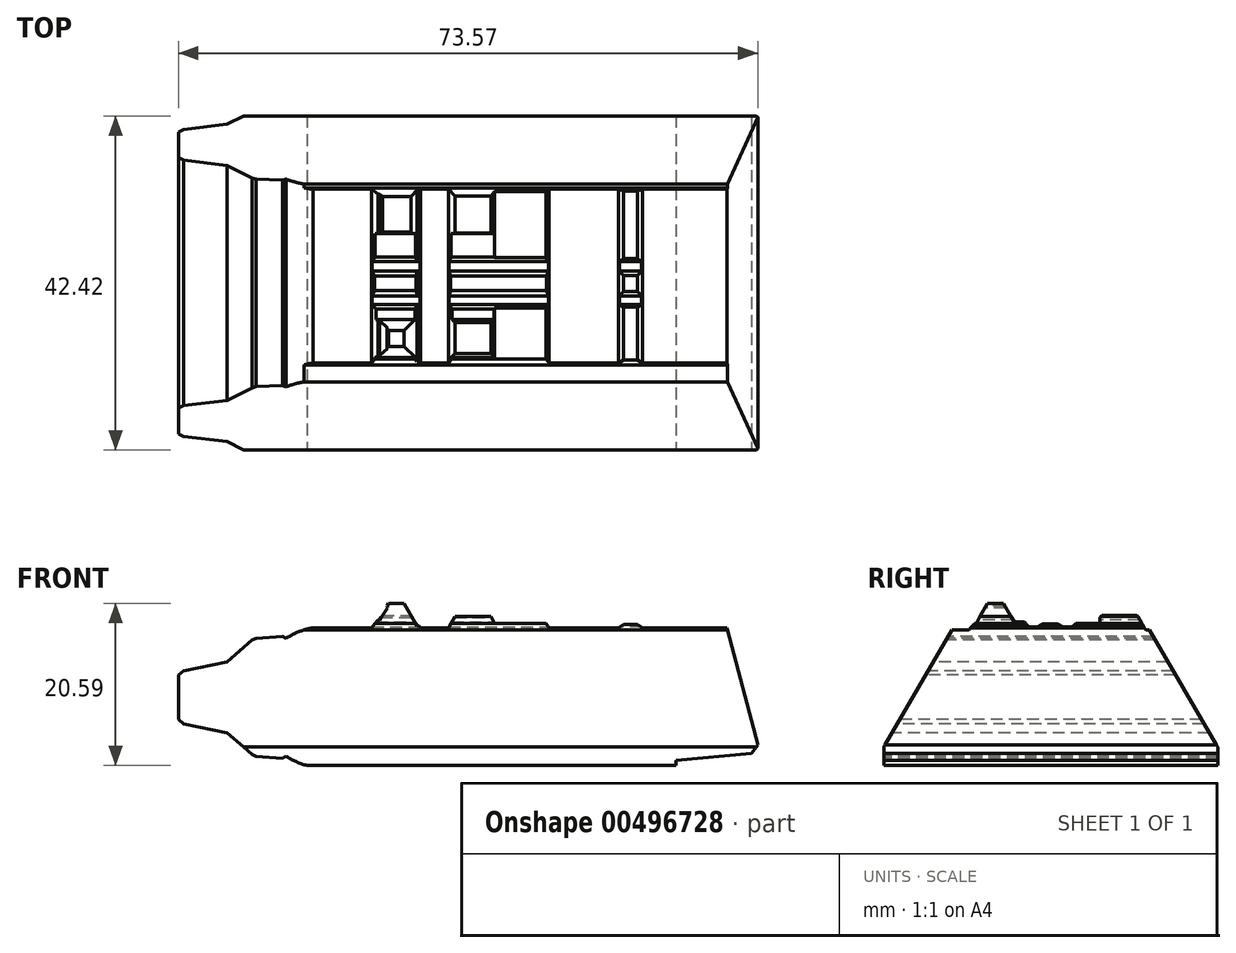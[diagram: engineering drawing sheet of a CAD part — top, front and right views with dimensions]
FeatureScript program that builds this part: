
annotation { "Feature Type Name" : "Feature", "Feature Type Description" : "" }
export const myFeature = defineFeature(function(context is Context, id is Id, definition is map)
    precondition{}
    {
        {
            var Q0;
            Q0=qCreatedBy(makeId("Top.planeOp"),FACE);
            var sketch = newSketch(context, id + "F0", { "sketchPlane" : qUnion([Q0])});
            skLineSegment(sketch, "E0", {"start": v(30.01, -20.73) * mm, "end": v(-121.62, -20.73) * mm, "construction": true});
            skLineSegment(sketch, "E1", {"start": v(-11.64, 108.22) * mm, "end": v(32.5, 108.22) * mm, "construction": true});
            skLineSegment(sketch, "E2", {"start": v(19.72, 67.84) * mm, "end": v(19.72, 108.22) * mm, "construction": true});
            skLineSegment(sketch, "E3", {"start": v(3.91, 88.98) * mm, "end": v(38.78, 88.98) * mm, "construction": true});
            skLineSegment(sketch, "E4", {"start": v(19.72, 67.84) * mm, "end": v(19.72, 88.98) * mm, "construction": true});
            skLineSegment(sketch, "E5", {"start": v(10.58, 90.44) * mm, "end": v(38.78, 90.44) * mm, "construction": true});
            skLineSegment(sketch, "E6", {"start": v(19.72, 90.44) * mm, "end": v(19.72, 67.84) * mm});
            skPoint(sketch, "E7", {"position": v(18.71, -41.94) * mm});
            skLineSegment(sketch, "E8", {"start": v(18.71, -41.94) * mm, "end": v(-45.8, -41.94) * mm});
            skLineSegment(sketch, "E9", {"start": v(-45.8, -41.94) * mm, "end": v(-45.8, -20.73) * mm});
            skLineSegment(sketch, "E10", {"start": v(18.71, -41.94) * mm, "end": v(18.71, -20.73) * mm});
            skLineSegment(sketch, "E11", {"start": v(18.71, -20.73) * mm, "end": v(-45.8, -20.73) * mm});
            skLineSegment(sketch, "E12.MirrorCS", {"start": v(-45.8, 0.48) * mm, "end": v(-45.8, -20.73) * mm});
            skLineSegment(sketch, "E13.MirrorCS", {"start": v(18.71, 0.48) * mm, "end": v(-45.8, 0.48) * mm});
            skLineSegment(sketch, "E14.MirrorCS", {"start": v(18.71, 0.48) * mm, "end": v(18.71, -20.73) * mm});
            skLineSegment(sketch, "E15", {"start": v(-56.07, -20.73) * mm, "end": v(-56.07, -41.94) * mm});
            skLineSegment(sketch, "E16", {"start": v(-56.07, -41.94) * mm, "end": v(-45.8, -41.94) * mm});
            skLineSegment(sketch, "E17.MirrorCS", {"start": v(-56.07, -20.73) * mm, "end": v(-56.07, 0.48) * mm});
            skLineSegment(sketch, "E18.MirrorCS", {"start": v(-56.07, 0.48) * mm, "end": v(-45.8, 0.48) * mm});
            skSolve(sketch);
        }
        {
            var Q0;
            Q0=makeQuery(id+"F0.imprint","IMPRINT",FACE,{"disambiguationData":[TD([[makeQuery(id+"F0.imprint","IMPRINT",EDGE,{"derivedFrom":sQuery(id+"F0.wireOp",EDGE,"E11")}),-1.0]])]});
            var Q1;
            Q1=makeQuery(id+"F0.imprint","IMPRINT",FACE,{"disambiguationData":[TD([[makeQuery(id+"F0.imprint","IMPRINT",EDGE,{"derivedFrom":sQuery(id+"F0.wireOp",EDGE,"E8")}),-1.0]])]});
            var Q2;
            Q2=makeQuery(id+"F0.imprint","IMPRINT",FACE,{"disambiguationData":[TD([[makeQuery(id+"F0.imprint","IMPRINT",EDGE,{"derivedFrom":sQuery(id+"F0.wireOp",EDGE,"E9")}),1.0]])]});
            extrude(context, id + "F1", {"entities" : qUnion([Q0, Q1, Q2]), "depth" : 25.4 * mm});
        }
        {
            var Q0;
            Q0=makeQuery(id+"F1.opExtrude","SWEPT_FACE",FACE,{"disambiguationData":[OSD([sQuery(id+"F0.wireOp",EDGE,"E8")])]});
            var sketch = newSketch(context, id + "F2", { "sketchPlane" : qUnion([Q0])});
            skLineSegment(sketch, "E19", {"start": v(-38.72, 17.5) * mm, "end": v(13.85, 17.5) * mm});
            skLineSegment(sketch, "E20", {"start": v(13.85, 17.5) * mm, "end": v(17.78, 2.64) * mm});
            skLineSegment(sketch, "E21", {"start": v(17.78, 2.64) * mm, "end": v(17.01, 1.56) * mm});
            skLineSegment(sketch, "E22", {"start": v(17.01, 1.56) * mm, "end": v(7.37, 0.66) * mm});
            skLineSegment(sketch, "E23", {"start": v(7.37, 0.66) * mm, "end": v(7.37, -0.21) * mm});
            skLineSegment(sketch, "E24", {"start": v(7.37, -0.21) * mm, "end": v(-38.4, -0.21) * mm});
            skArc(sketch, "E25", {"start": v(-38.72, 17.5) * mm, "mid": v(-46.17, 8.5) * mm, "end": v(-38.4, -0.21) * mm});
            skLineSegment(sketch, "E26", {"start": v(-37.2, 8.67) * mm, "end": v(-57.94, 8.67) * mm, "construction": true});
            skLineSegment(sketch, "E27", {"start": v(-42.17, 16.13) * mm, "end": v(-42.58, 16.41) * mm});
            skLineSegment(sketch, "E28", {"start": v(-42.61, 16.42) * mm, "end": v(-45.95, 16.16) * mm});
            skPoint(sketch, "E29.visualSharp", {"position": v(-42.6, 16.42) * mm});
            skArc(sketch, "E29.filletArc", {"start": v(-42.58, 16.41) * mm, "mid": v(-42.6, 16.42) * mm, "end": v(-42.61, 16.42) * mm});
            skLineSegment(sketch, "E30.MirrorCS", {"start": v(-42.61, 0.91) * mm, "end": v(-45.95, 1.17) * mm});
            skLineSegment(sketch, "E31.MirrorCS", {"start": v(-42.17, 1.2) * mm, "end": v(-42.58, 0.92) * mm});
            skArc(sketch, "E32", {"start": v(-44.02, 16.31) * mm, "mid": v(-47.2, 8.7) * mm, "end": v(-44.15, 1.03) * mm});
            skArc(sketch, "E33", {"start": v(-45.95, 16.16) * mm, "mid": v(-48.83, 8.67) * mm, "end": v(-45.95, 1.17) * mm});
            skLineSegment(sketch, "E34", {"start": v(-45.95, 16.16) * mm, "end": v(-46.43, 15.92) * mm});
            skLineSegment(sketch, "E35", {"start": v(-46.43, 15.92) * mm, "end": v(-49.61, 13.17) * mm});
            skLineSegment(sketch, "E36", {"start": v(-49.61, 13.17) * mm, "end": v(-55.16, 12.03) * mm});
            skLineSegment(sketch, "E37", {"start": v(-55.16, 12.03) * mm, "end": v(-55.79, 11.48) * mm});
            skLineSegment(sketch, "E38", {"start": v(-55.79, 11.48) * mm, "end": v(-55.79, 8.67) * mm});
            skLineSegment(sketch, "E39.MirrorCS", {"start": v(-49.61, 4.17) * mm, "end": v(-55.16, 5.3) * mm});
            skLineSegment(sketch, "E40.MirrorCS", {"start": v(-55.16, 5.3) * mm, "end": v(-55.79, 5.85) * mm});
            skLineSegment(sketch, "E41.MirrorCS", {"start": v(-55.79, 5.85) * mm, "end": v(-55.79, 8.67) * mm});
            skLineSegment(sketch, "E42.MirrorCS", {"start": v(-46.43, 1.41) * mm, "end": v(-49.61, 4.17) * mm});
            skLineSegment(sketch, "E43.MirrorCS", {"start": v(-45.95, 1.17) * mm, "end": v(-46.43, 1.41) * mm});
            skLineSegment(sketch, "E44", {"start": v(-31.25, 17.5) * mm, "end": v(-30.46, 18.52) * mm});
            skLineSegment(sketch, "E45", {"start": v(-30.46, 18.52) * mm, "end": v(-30.28, 18.52) * mm});
            skLineSegment(sketch, "E46", {"start": v(-30.28, 18.52) * mm, "end": v(-29.25, 20.03) * mm});
            skLineSegment(sketch, "E47", {"start": v(-29.25, 20.03) * mm, "end": v(-29.34, 20.3) * mm});
            skLineSegment(sketch, "E48", {"start": v(-29.34, 20.3) * mm, "end": v(-29.12, 20.59) * mm});
            skLineSegment(sketch, "E49", {"start": v(-29.12, 20.59) * mm, "end": v(-27.14, 20.59) * mm});
            skLineSegment(sketch, "E50", {"start": v(-27.14, 20.59) * mm, "end": v(-25.47, 17.7) * mm});
            skLineSegment(sketch, "E51", {"start": v(-25.47, 17.7) * mm, "end": v(-25.23, 17.7) * mm});
            skLineSegment(sketch, "E52", {"start": v(-25.23, 17.7) * mm, "end": v(-25.05, 17.5) * mm});
            skLineSegment(sketch, "E53", {"start": v(-21.5, 17.5) * mm, "end": v(-20.66, 18.93) * mm});
            skLineSegment(sketch, "E54", {"start": v(-20.66, 18.93) * mm, "end": v(-16.12, 18.93) * mm});
            skLineSegment(sketch, "E55", {"start": v(-16.12, 18.93) * mm, "end": v(-15.63, 18.04) * mm});
            skLineSegment(sketch, "E56", {"start": v(-15.63, 18.04) * mm, "end": v(-9.11, 18.04) * mm});
            skLineSegment(sketch, "E57", {"start": v(-9.11, 18.04) * mm, "end": v(-8.75, 17.5) * mm});
            skLineSegment(sketch, "E58", {"start": v(0.11, 17.5) * mm, "end": v(0.72, 17.92) * mm});
            skLineSegment(sketch, "E59", {"start": v(0.72, 17.92) * mm, "end": v(2.53, 17.92) * mm});
            skLineSegment(sketch, "E60", {"start": v(2.53, 17.92) * mm, "end": v(3.15, 17.5) * mm});
            skLineSegment(sketch, "E61", {"start": v(-45.95, 16.16) * mm, "end": v(-42.58, 16.41) * mm});
            skLineSegment(sketch, "E62", {"start": v(-45.95, 1.17) * mm, "end": v(-42.58, 0.92) * mm});
            skLineSegment(sketch, "E63", {"start": v(-55.16, 12.03) * mm, "end": v(-49.61, 13.17) * mm});
            skLineSegment(sketch, "E64", {"start": v(-45.95, 16.16) * mm, "end": v(-42.61, 16.42) * mm});
            skSolve(sketch);
        }
        {
            var Q0;
            {var subQ1=sQuery(id+"F2.wireOp",EDGE,"E30.MirrorCS");var subQ3=sQuery(id+"F2.wireOp",EDGE,"E32");var subQ4=makeQuery(id+"F2.imprint","INTERSECT",VERTEX,{"derivedFrom":[subQ1,subQ3]});Q0=makeQuery(id+"F2.imprint","IMPRINT",FACE,{"disambiguationData":[TD([[makeQuery(id+"F2.imprint","IMPRINT",EDGE,{"disambiguationData":[TD([[subQ4,1.0]])],"derivedFrom":subQ3}),-1.0]])]});}
            var Q1;
            {var subQ0=sQuery(id+"F2.wireOp",EDGE,"E29.filletArc");Q1=makeQuery(id+"F2.imprint","IMPRINT",FACE,{"disambiguationData":[TD([[makeQuery(id+"F2.imprint","IMPRINT",EDGE,{"derivedFrom":subQ0}),1.0]])]});}
            var Q2;
            {var subQ0=sQuery(id+"F2.wireOp",EDGE,"E64");var subQ1=sQuery(id+"F2.wireOp",EDGE,"E32");var subQ2=makeQuery(id+"F2.imprint","INTERSECT",VERTEX,{"derivedFrom":[subQ1,subQ0]});Q2=makeQuery(id+"F2.imprint","IMPRINT",FACE,{"disambiguationData":[TD([[makeQuery(id+"F2.imprint","IMPRINT",EDGE,{"disambiguationData":[TD([[subQ2,-1.0]])],"derivedFrom":subQ1}),-1.0]])]});}
            var Q3;
            {var subQ0=sQuery(id+"F2.wireOp",EDGE,"E24");Q3=makeQuery(id+"F2.imprint","IMPRINT",FACE,{"disambiguationData":[TD([[makeQuery(id+"F2.imprint","IMPRINT",EDGE,{"derivedFrom":subQ0}),-1.0]])]});}
            var Q4;
            {var subQ9=sQuery(id+"F2.wireOp",EDGE,"E20");Q4=makeQuery(id+"F2.imprint","IMPRINT",FACE,{"disambiguationData":[TD([[makeQuery(id+"F2.imprint","IMPRINT",EDGE,{"derivedFrom":subQ9}),1.0]])]});}
            extrude(context, id + "F3", {"entities" : qUnion([Q0, Q1, Q2, Q3, Q4]), "operationType" : NewBodyOperationType.REMOVE, "oppositeDirection" : true, "depth" : 51.82 * mm});
        }
        {
            var Q0;
            Q0=qCreatedBy(makeId("Right.planeOp"),FACE);
            var sketch = newSketch(context, id + "F4", { "sketchPlane" : qUnion([Q0])});
            skPoint(sketch, "E65.0", {"position": v(-20.73, 17.5) * mm});
            skLineSegment(sketch, "E66", {"start": v(-20.73, 17.5) * mm, "end": v(-20.73, -3.08) * mm, "construction": true});
            skLineSegment(sketch, "E67", {"start": v(-20.73, 17.23) * mm, "end": v(-33.29, 17.23) * mm});
            skLineSegment(sketch, "E68", {"start": v(-33.29, 17.23) * mm, "end": v(-42.28, 1.8) * mm});
            skLineSegment(sketch, "E69", {"start": v(-42.28, 1.8) * mm, "end": v(-42.28, -0.16) * mm});
            skLineSegment(sketch, "E70", {"start": v(-42.28, -0.16) * mm, "end": v(-42.08, -0.16) * mm});
            skLineSegment(sketch, "E71", {"start": v(-42.08, -0.16) * mm, "end": v(-42.08, -0.51) * mm});
            skLineSegment(sketch, "E72", {"start": v(-42.08, -0.51) * mm, "end": v(-20.73, -0.51) * mm});
            skLineSegment(sketch, "E73", {"start": v(-31.14, 17.23) * mm, "end": v(-30.37, 18.06) * mm});
            skLineSegment(sketch, "E74", {"start": v(-30.37, 18.06) * mm, "end": v(-30.19, 18.06) * mm});
            skLineSegment(sketch, "E75", {"start": v(-30.19, 18.06) * mm, "end": v(-28.74, 20.64) * mm});
            skLineSegment(sketch, "E76", {"start": v(-28.74, 20.64) * mm, "end": v(-26.79, 20.64) * mm});
            skLineSegment(sketch, "E77", {"start": v(-26.79, 20.64) * mm, "end": v(-25.34, 18.22) * mm});
            skLineSegment(sketch, "E78", {"start": v(-25.34, 18.22) * mm, "end": v(-24.06, 18.22) * mm});
            skLineSegment(sketch, "E79", {"start": v(-24.06, 18.22) * mm, "end": v(-23.46, 17.57) * mm});
            skLineSegment(sketch, "E80", {"start": v(-23.46, 17.57) * mm, "end": v(-23.46, 17.23) * mm});
            skLineSegment(sketch, "E81", {"start": v(-23.46, 17.57) * mm, "end": v(-22.4, 17.57) * mm});
            skLineSegment(sketch, "E82", {"start": v(-22.4, 17.57) * mm, "end": v(-21.72, 17.99) * mm});
            skLineSegment(sketch, "E83", {"start": v(-21.72, 17.99) * mm, "end": v(-19.87, 17.99) * mm});
            skLineSegment(sketch, "E84", {"start": v(-19.87, 17.99) * mm, "end": v(-19.2, 17.57) * mm});
            skLineSegment(sketch, "E85", {"start": v(-19.2, 17.57) * mm, "end": v(-18.01, 17.57) * mm});
            skLineSegment(sketch, "E86", {"start": v(-18.01, 17.57) * mm, "end": v(-17.46, 18.08) * mm});
            skLineSegment(sketch, "E87", {"start": v(-17.46, 18.08) * mm, "end": v(-14.46, 18.08) * mm});
            skLineSegment(sketch, "E88", {"start": v(-14.46, 18.08) * mm, "end": v(-14.46, 18.8) * mm});
            skLineSegment(sketch, "E89", {"start": v(-14.46, 18.8) * mm, "end": v(-14.25, 19.07) * mm});
            skLineSegment(sketch, "E90", {"start": v(-14.25, 19.07) * mm, "end": v(-9.75, 19.07) * mm});
            skLineSegment(sketch, "E91.MirrorCS", {"start": v(-20.73, 17.23) * mm, "end": v(-8.16, 17.23) * mm});
            skLineSegment(sketch, "E92.MirrorCS", {"start": v(-8.16, 17.23) * mm, "end": v(0.83, 1.8) * mm});
            skLineSegment(sketch, "E93.MirrorCS", {"start": v(0.83, 1.8) * mm, "end": v(0.83, -0.16) * mm});
            skLineSegment(sketch, "E94.MirrorCS", {"start": v(0.63, -0.16) * mm, "end": v(0.63, -0.51) * mm});
            skLineSegment(sketch, "E95.MirrorCS", {"start": v(0.63, -0.51) * mm, "end": v(-20.73, -0.51) * mm});
            skLineSegment(sketch, "E96", {"start": v(-9.75, 19.07) * mm, "end": v(-8.66, 17.23) * mm});
            skLineSegment(sketch, "E97", {"start": v(0.63, -0.16) * mm, "end": v(0.83, -0.16) * mm});
            skLineSegment(sketch, "E98", {"start": v(-42.28, 1.8) * mm, "end": v(-42.28, 21.25) * mm});
            skLineSegment(sketch, "E99", {"start": v(-42.28, 21.25) * mm, "end": v(1.26, 21.25) * mm});
            skLineSegment(sketch, "E100", {"start": v(1.26, 21.25) * mm, "end": v(0.83, 1.8) * mm});
            skLineSegment(sketch, "E101", {"start": v(0.83, -0.16) * mm, "end": v(0.83, -0.51) * mm});
            skLineSegment(sketch, "E102", {"start": v(0.83, -0.51) * mm, "end": v(0.63, -0.51) * mm});
            skLineSegment(sketch, "E103", {"start": v(-42.28, -0.16) * mm, "end": v(-42.28, -0.51) * mm});
            skLineSegment(sketch, "E104", {"start": v(-42.28, -0.51) * mm, "end": v(-42.08, -0.51) * mm});
            skSolve(sketch);
        }
        {
            var Q0;
            {var subQ4=sQuery(id+"F4.wireOp",EDGE,"E68");Q0=makeQuery(id+"F4.imprint","IMPRINT",FACE,{"disambiguationData":[TD([[makeQuery(id+"F4.imprint","IMPRINT",EDGE,{"derivedFrom":subQ4}),-1.0]])]});}
            extrude(context, id + "F5", {"entities" : qUnion([Q0]), "operationType" : NewBodyOperationType.REMOVE, "oppositeDirection" : true, "depth" : 78.49 * mm});
        }
        {
            var Q0;
            {var subQ4=sQuery(id+"F4.wireOp",EDGE,"E68");Q0=makeQuery(id+"F4.imprint","IMPRINT",FACE,{"disambiguationData":[TD([[makeQuery(id+"F4.imprint","IMPRINT",EDGE,{"derivedFrom":subQ4}),-1.0]])]});}
            extrude(context, id + "F6", {"entities" : qUnion([Q0]), "operationType" : NewBodyOperationType.REMOVE, "depth" : 43.18 * mm});
        }
    });
